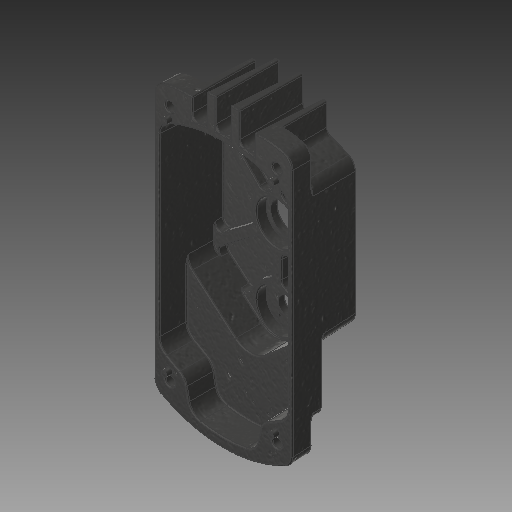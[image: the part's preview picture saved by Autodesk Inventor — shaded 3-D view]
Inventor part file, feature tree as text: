
AUTODESK INVENTOR PART (.ipt)
format: ipt  version: 2018 (Build 220112000, 112)  size: 3,718,656 bytes
history: native  units: in
note: dims shown in document units (in); Inventor stores cm internally (conversion verified against a paired STEP export)
features: other x2, fillet x1
ambient origin geometry x8: Origin, YZ Plane, XZ Plane, XY Plane, X Axis, Y Axis, Z Axis, Center Point
bodies: Solid1 (feature_tree), Solid2 (feature_tree), Solid3 (feature_tree)
feature tree (3):
  fillet  "Fillet49"  [1 undecoded]
  other  "_AM Logo_-_Boss-Extrude4_"
  other  "_AM Logo_-_Boss-Extrude4_:1"
note: 1 required parameter value undecoded (feature->parameter linkage not recoverable at this tier; creation-order binding heuristic only, values carry confidence <= 0.55)
